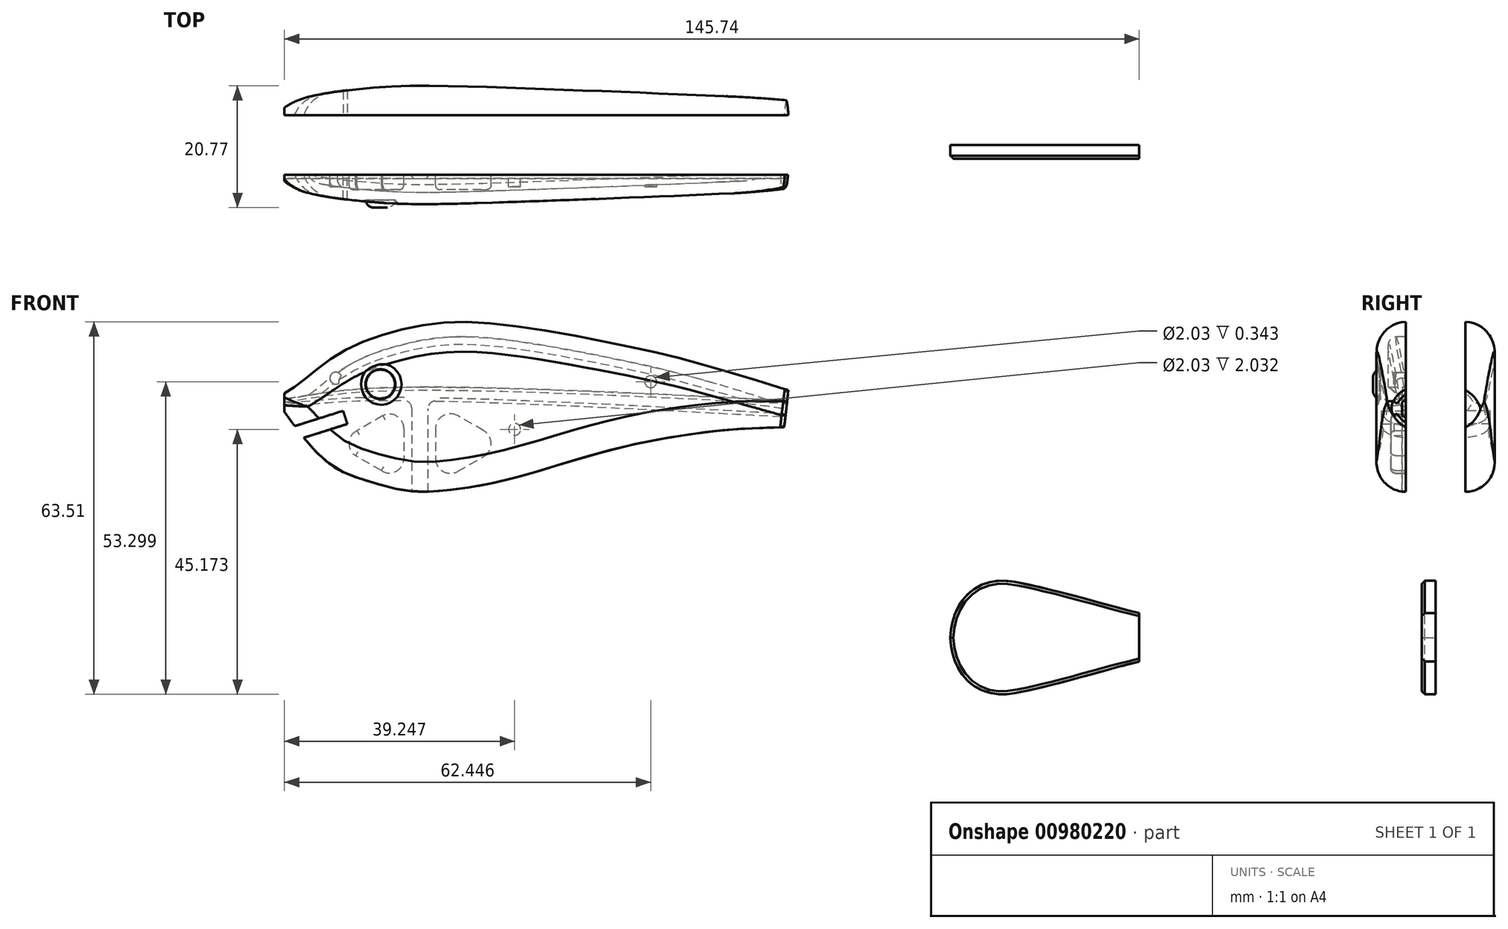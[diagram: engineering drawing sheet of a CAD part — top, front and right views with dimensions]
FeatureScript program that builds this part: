
annotation { "Feature Type Name" : "Feature", "Feature Type Description" : "" }
export const myFeature = defineFeature(function(context is Context, id is Id, definition is map)
    precondition{}
    {
        {
            var Q0;
            Q0=qCreatedBy(makeId("Front.planeOp"),FACE);
            var sketch = newSketch(context, id + "F0", { "sketchPlane" : qUnion([Q0])});
            skLineSegment(sketch, "E0", {"start": v(-42.86, 0) * mm, "end": v(42.86, 0) * mm});
            skSolve(sketch);
        }
        {
            var Q0;
            Q0=qCreatedBy(makeId("Front.planeOp"),FACE);
            var sketch = newSketch(context, id + "F1", { "sketchPlane" : qUnion([Q0])});
            skLineSegment(sketch, "E1", {"start": v(-42.86, -1.4) * mm, "end": v(-42.86, 1.77) * mm});
            skFitSpline(sketch, "E2", {"points": [v(-42.86, 1.77) * mm, v(-40.35, 3.39) * mm, v(-36.78, 6.26) * mm, v(-31.29, 9.73) * mm, v(-23.44, 12.5) * mm, v(-14.52, 13.9) * mm, v(-2.07, 13) * mm, v(15.45, 9.8) * mm, v(27.42, 6.96) * mm, v(43.06, 2.27) * mm], "startDerivative": vector(39.21, 23.39) * mm, "endDerivative": vector(112.18, -34.84) * mm});
            skLineSegment(sketch, "E3", {"start": v(43.06, 2.27) * mm, "end": v(42.36, -4.04) * mm});
            skFitSpline(sketch, "E4", {"points": [v(42.36, -4.04) * mm, v(32.37, -4.52) * mm, v(17.64, -6.76) * mm, v(5.02, -10.13) * mm, v(-6.94, -13.46) * mm, v(-16.36, -14.9) * mm, v(-21.97, -14.86) * mm, v(-29.24, -13.02) * mm, v(-34.41, -10.79) * mm, v(-38.97, -6.54) * mm, v(-42.86, -1.4) * mm], "startDerivative": vector(-88.65, -2.09) * mm, "endDerivative": vector(-43.74, 61.13) * mm});
            skSolve(sketch);
        }
        {
            var Q0;
            Q0 = qSketchRegion(id + "F1", true);
            extrude(context, id + "F2", {"entities" : qUnion([Q0]), "depth" : 10.16 * mm, "offsetDistance" : 25.4 * mm});
        }
        {
            var Q0;
            Q0=qCreatedBy(makeId("Top.planeOp"),FACE);
            var sketch = newSketch(context, id + "F3", { "sketchPlane" : qUnion([Q0])});
            skLineSegment(sketch, "E5", {"start": v(-42.86, 0) * mm, "end": v(-42.86, -3.14) * mm});
            skFitSpline(sketch, "E6", {"points": [v(-42.86, -3.14) * mm, v(-36.68, -1.52) * mm, v(-25.95, -0.28) * mm, v(-17.83, -0.07) * mm, v(-1.73, -0.51) * mm, v(26.04, -1.58) * mm, v(43.3, -2.37) * mm], "startDerivative": vector(48.92, 15.17) * mm, "endDerivative": vector(84.45, -4.03) * mm});
            skLineSegment(sketch, "E7", {"start": v(-42.86, 0) * mm, "end": v(-42.86, 3.25) * mm});
            skLineSegment(sketch, "E8", {"start": v(-42.86, 3.25) * mm, "end": v(43.3, 3.25) * mm});
            skLineSegment(sketch, "E9", {"start": v(43.3, 3.25) * mm, "end": v(43.3, -2.37) * mm});
            skFitSpline(sketch, "E10.MirrorCS", {"points": [v(-42.86, -7.02) * mm, v(-36.68, -8.64) * mm, v(-25.95, -9.88) * mm, v(-17.83, -10.1) * mm, v(-1.73, -9.65) * mm, v(26.04, -8.58) * mm, v(43.3, -7.79) * mm], "startDerivative": vector(48.92, -15.17) * mm, "endDerivative": vector(84.45, 4.03) * mm});
            skLineSegment(sketch, "E11.MirrorCS", {"start": v(-42.86, -7.02) * mm, "end": v(-42.86, -13.4) * mm});
            skLineSegment(sketch, "E12.MirrorCS", {"start": v(-42.86, -13.4) * mm, "end": v(43.3, -13.4) * mm});
            skLineSegment(sketch, "E13.MirrorCS", {"start": v(43.3, -13.4) * mm, "end": v(43.3, -7.79) * mm});
            skSolve(sketch);
        }
        {
            var Q0;
            Q0 = qSketchRegion(id + "F3", true);
            extrude(context, id + "F4", {"entities" : qUnion([Q0]), "operationType" : NewBodyOperationType.REMOVE, "endBound" : BoundingType.SYMMETRIC, "oppositeDirection" : true, "depth" : 152.4 * mm, "offsetDistance" : 25.4 * mm});
        }
        {
            var Q0;
            Q0=qCreatedBy(makeId("Top.planeOp"),FACE);
            var sketch = newSketch(context, id + "F5", { "sketchPlane" : qUnion([Q0])});
            skLineSegment(sketch, "E14.bottom", {"start": v(-44.5, -5.08) * mm, "end": v(45.7, -5.08) * mm});
            skLineSegment(sketch, "E14.top", {"start": v(-44.5, 11.17) * mm, "end": v(45.7, 11.17) * mm});
            skLineSegment(sketch, "E14.left", {"start": v(-44.5, -5.08) * mm, "end": v(-44.5, 11.17) * mm});
            skLineSegment(sketch, "E14.right", {"start": v(45.7, -5.08) * mm, "end": v(45.7, 11.17) * mm});
            skSolve(sketch);
        }
        {
            var Q0;
            Q0 = qSketchRegion(id + "F5", true);
            extrude(context, id + "F6", {"entities" : qUnion([Q0]), "operationType" : NewBodyOperationType.REMOVE, "endBound" : BoundingType.SYMMETRIC, "oppositeDirection" : true, "depth" : 152.4 * mm, "offsetDistance" : 25.4 * mm});
        }
        {
            var Q0;
            Q0=makeQuery(id+"F4.boolean.opBoolean","INTERSECT",EDGE,{"derivedFrom":[makeQuery(id+"F2.opExtrude","SWEPT_FACE",FACE,{"disambiguationData":[OSD([sQuery(id+"F1.wireOp",EDGE,"E2")])]}),makeQuery(id+"F4.opExtrude","SWEPT_FACE",FACE,{"disambiguationData":[OSD([sQuery(id+"F3.wireOp",EDGE,"E10.MirrorCS")])]})]});
            var Q1;
            Q1=makeQuery(id+"F4.boolean.opBoolean","INTERSECT",EDGE,{"derivedFrom":[makeQuery(id+"F2.opExtrude","SWEPT_FACE",FACE,{"disambiguationData":[OSD([sQuery(id+"F1.wireOp",EDGE,"E4")])]}),makeQuery(id+"F4.opExtrude","SWEPT_FACE",FACE,{"disambiguationData":[OSD([sQuery(id+"F3.wireOp",EDGE,"E10.MirrorCS")])]})]});
            fillet(context, id + "F7", {"entities" : qUnion([Q0, Q1]), "radius" : 5.08 * mm, "tangentPropagation" : true, "allowEdgeOverflow" : false});
        }
        {
            var Q0;
            Q0=qCreatedBy(makeId("Front.planeOp"),FACE);
            var sketch = newSketch(context, id + "F8", { "sketchPlane" : qUnion([Q0])});
            skLineSegment(sketch, "E15", {"start": v(-32.84, -1.24) * mm, "end": v(-47.55, -5.87) * mm});
            skLineSegment(sketch, "E16", {"start": v(-47.55, -5.87) * mm, "end": v(-46.84, -8.13) * mm});
            skLineSegment(sketch, "E17", {"start": v(-46.84, -8.13) * mm, "end": v(-32.13, -3.49) * mm});
            skLineSegment(sketch, "E18", {"start": v(-32.13, -3.49) * mm, "end": v(-32.84, -1.24) * mm});
            skSolve(sketch);
        }
        {
            var Q0;
            Q0 = qSketchRegion(id + "F8", true);
            extrude(context, id + "F9", {"entities" : qUnion([Q0]), "operationType" : NewBodyOperationType.REMOVE, "depth" : 25.4 * mm, "offsetDistance" : 25.4 * mm});
        }
        {
            var Q0;
            Q0=makeQuery(id+"F2.opExtrude","SWEPT_BODY",BODY,{"disambiguationData":[OSD([sQuery(id+"F1.wireOp",EDGE,"E1"),sQuery(id+"F1.wireOp",EDGE,"E2"),sQuery(id+"F1.wireOp",EDGE,"E3"),sQuery(id+"F1.wireOp",EDGE,"E4")])]});
            var Q1;
            Q1=qCreatedBy(makeId("Front.planeOp"),FACE);
            mirror(context, id + "F10", {"entities" : qUnion([Q0]), "mirrorPlane" : qUnion([Q1])});
        }
        {
            var Q0;
            Q0=qCreatedBy(makeId("Front.planeOp"),FACE);
            var sketch = newSketch(context, id + "F11", { "sketchPlane" : qUnion([Q0])});
            skLineSegment(sketch, "E19", {"start": v(102.87, -39.86) * mm, "end": v(102.87, -35.72) * mm});
            skFitSpline(sketch, "E20", {"points": [v(102.87, -35.72) * mm, v(94.2, -33.44) * mm, v(85.73, -31.27) * mm, v(82.22, -30.53) * mm, v(78.88, -30.22) * mm, v(75.16, -31.35) * mm, v(72.53, -33.83) * mm, v(71.19, -36.7) * mm, v(70.67, -39.9) * mm], "startDerivative": vector(-48.37, 11.41) * mm, "endDerivative": vector(-0.62, -33.43) * mm});
            skLineSegment(sketch, "E21", {"start": v(70.67, -39.9) * mm, "end": v(102.87, -39.86) * mm});
            skFitSpline(sketch, "E22.MirrorCS", {"points": [v(102.88, -44) * mm, v(94.22, -46.3) * mm, v(85.76, -48.5) * mm, v(82.25, -49.25) * mm, v(78.91, -49.57) * mm, v(75.2, -48.46) * mm, v(72.56, -45.98) * mm, v(71.2, -43.1) * mm, v(70.67, -39.9) * mm], "startDerivative": vector(-48.33, -11.57) * mm, "endDerivative": vector(-0.73, 33.43) * mm});
            skLineSegment(sketch, "E23.MirrorCS", {"start": v(102.87, -39.86) * mm, "end": v(102.88, -44) * mm});
            skSolve(sketch);
        }
        {
            var Q0;
            Q0 = qSketchRegion(id + "F11", true);
            extrude(context, id + "F12", {"entities" : qUnion([Q0]), "depth" : 2.34 * mm, "offsetDistance" : 25.4 * mm});
        }
        {
            var Q0;
            Q0=makeQuery(id+"F6.boolean.opBoolean","COPY",FACE,{"derivedFrom":makeQuery(id+"F6.opExtrude","SWEPT_FACE",FACE,{"disambiguationData":[OSD([sQuery(id+"F5.wireOp",EDGE,"E14.bottom")])]})});
            var sketch = newSketch(context, id + "F13", { "sketchPlane" : qUnion([Q0])});
            skLineSegment(sketch, "E24", {"start": v(42.86, 0.76) * mm, "end": v(42.86, -0.5) * mm});
            skLineSegment(sketch, "E25", {"start": v(-42.86, 0.5) * mm, "end": v(-42.56, -2.27) * mm});
            skFitSpline(sketch, "E26", {"points": [v(42.86, 0.76) * mm, v(28.16, 2.6) * mm, v(-42.86, 0.5) * mm], "startDerivative": vector(-45.97, 6.78) * mm, "endDerivative": vector(-118.14, -6) * mm});
            skFitSpline(sketch, "E27", {"points": [v(42.86, -0.5) * mm, v(28.16, 0.5) * mm, v(-42.56, -2.27) * mm], "startDerivative": vector(-46.03, 4.16) * mm, "endDerivative": vector(-117.54, -6.6) * mm});
            skLineSegment(sketch, "E28", {"start": v(18.37, -17.26) * mm, "end": v(18.37, -0.84) * mm});
            skLineSegment(sketch, "E29", {"start": v(21.17, -0.75) * mm, "end": v(21.17, -17.26) * mm});
            skLineSegment(sketch, "E30", {"start": v(21.17, -17.26) * mm, "end": v(18.37, -17.26) * mm});
            skFitSpline(sketch, "E31.trimOffspring", {"points": [v(42.86, -0.5) * mm, v(28.16, 0.5) * mm, v(-42.56, -2.27) * mm], "startDerivative": vector(-46.03, 4.16) * mm, "endDerivative": vector(-117.54, -6.6) * mm});
            skPoint(sketch, "E32.visualSharp", {"position": v(18.37, 0.46) * mm});
            skArc(sketch, "E32.filletArc", {"start": v(18.37, -0.84) * mm, "mid": v(18, 0.07) * mm, "end": v(17.08, 0.43) * mm});
            skPoint(sketch, "E33.visualSharp", {"position": v(21.17, 0.5) * mm});
            skArc(sketch, "E33.filletArc", {"start": v(22.43, 0.52) * mm, "mid": v(21.54, 0.14) * mm, "end": v(21.17, -0.75) * mm});
            skSolve(sketch);
        }
        {
            var Q0;
            Q0 = qSketchRegion(id + "F13", true);
            extrude(context, id + "F14", {"entities" : qUnion([Q0]), "operationType" : NewBodyOperationType.REMOVE, "oppositeDirection" : true, "depth" : 0.64 * mm, "offsetDistance" : 25.4 * mm});
        }
        {
            var Q0;
            Q0=makeQuery(id+"F14.boolean.opBoolean","COPY",EDGE,{"derivedFrom":makeQuery(id+"F14.opExtrude","CAP_EDGE",EDGE,{"disambiguationData":[OSD([sQuery(id+"F13.wireOp",EDGE,"E26")])],"isStart":false})});
            var Q1;
            Q1=makeQuery(id+"F14.boolean.opBoolean","COPY",EDGE,{"derivedFrom":makeQuery(id+"F14.opExtrude","CAP_EDGE",EDGE,{"disambiguationData":[OSD([sQuery(id+"F13.wireOp",EDGE,"E27")])],"isStart":false})});
            var Q2;
            Q2=makeQuery(id+"F14.boolean.opBoolean","COPY",EDGE,{"derivedFrom":makeQuery(id+"F14.opExtrude","CAP_EDGE",EDGE,{"disambiguationData":[OSD([sQuery(id+"F13.wireOp",EDGE,"E32.filletArc")])],"isStart":false})});
            fillet(context, id + "F15", {"entities" : qUnion([Q0, Q1, Q2]), "radius" : 0.5 * mm, "tangentPropagation" : true, "allowEdgeOverflow" : false});
        }
        {
            var Q0;
            {var subQ0=makeQuery(id+"F4.opExtrude","SWEPT_FACE",FACE,{"disambiguationData":[OSD([sQuery(id+"F3.wireOp",EDGE,"E10.MirrorCS")])]});Q0=makeQuery(id+"F7.opFillet","BLEND_EDGE",EDGE,{"disambiguationData":[OD(0.0)],"blendedFrom":[makeQuery(id+"F4.boolean.opBoolean","INTERSECT",EDGE,{"derivedFrom":[makeQuery(id+"F2.opExtrude","SWEPT_FACE",FACE,{"disambiguationData":[OSD([sQuery(id+"F1.wireOp",EDGE,"E2")])]}),subQ0]}),makeQuery(id+"F4.boolean.opBoolean","INTERSECT",EDGE,{"derivedFrom":[makeQuery(id+"F2.opExtrude","SWEPT_FACE",FACE,{"disambiguationData":[OSD([sQuery(id+"F1.wireOp",EDGE,"E4")])]}),subQ0]})],"blendedInto":[]});}
            fillet(context, id + "F16", {"entities" : qUnion([Q0]), "radius" : 1.27 * mm, "tangentPropagation" : true, "allowEdgeOverflow" : false});
        }
        {
            var Q0;
            {var subQ0=makeQuery(id+"F4.opExtrude","SWEPT_FACE",FACE,{"disambiguationData":[OSD([sQuery(id+"F3.wireOp",EDGE,"E10.MirrorCS")])]});Q0=makeQuery(id+"F7.opFillet","BLEND_EDGE",EDGE,{"disambiguationData":[OD(1.0)],"blendedFrom":[makeQuery(id+"F4.boolean.opBoolean","INTERSECT",EDGE,{"derivedFrom":[makeQuery(id+"F2.opExtrude","SWEPT_FACE",FACE,{"disambiguationData":[OSD([sQuery(id+"F1.wireOp",EDGE,"E2")])]}),subQ0]}),makeQuery(id+"F4.boolean.opBoolean","INTERSECT",EDGE,{"derivedFrom":[makeQuery(id+"F2.opExtrude","SWEPT_FACE",FACE,{"disambiguationData":[OSD([sQuery(id+"F1.wireOp",EDGE,"E4")])]}),subQ0]})],"blendedInto":[]});}
            fillet(context, id + "F17", {"entities" : qUnion([Q0]), "radius" : 2.54 * mm, "tangentPropagation" : true, "allowEdgeOverflow" : false});
        }
        {
            var Q0;
            Q0=makeQuery(id+"F14.boolean.opBoolean","SPLIT",FACE,{"disambiguationData":[TD([makeQuery(id+"F14.opExtrude","SWEPT_FACE",FACE,{"disambiguationData":[OSD([sQuery(id+"F13.wireOp",EDGE,"E26")])]})])],"derivedFrom":makeQuery(id+"F6.boolean.opBoolean","COPY",FACE,{"derivedFrom":makeQuery(id+"F6.opExtrude","SWEPT_FACE",FACE,{"disambiguationData":[OSD([sQuery(id+"F5.wireOp",EDGE,"E14.bottom")])]})})});
            var sketch = newSketch(context, id + "F18", { "sketchPlane" : qUnion([Q0])});
            skFitSpline(sketch, "E34.0", {"points": [v(41.56, -0.41) * mm, v(41.36, -0.3) * mm, v(40.94, -0.04) * mm, v(40.28, 0.37) * mm, v(39.7, 0.74) * mm, v(39.22, 1.08) * mm, v(38.85, 1.34) * mm, v(38.48, 1.62) * mm, v(38, 2) * mm, v(37.4, 2.49) * mm, v(36.67, 3.09) * mm, v(35.7, 3.89) * mm, v(34.45, 4.86) * mm, v(32.82, 5.99) * mm, v(31.33, 6.86) * mm, v(30.07, 7.5) * mm, v(28.74, 8.11) * mm, v(26.95, 8.8) * mm, v(25.04, 9.42) * mm, v(23.48, 9.86) * mm, v(21.9, 10.27) * mm, v(19.93, 10.7) * mm, v(17.54, 11.1) * mm, v(15.5, 11.3) * mm, v(13.82, 11.38) * mm, v(12.08, 11.4) * mm, v(9.8, 11.32) * mm, v(6.86, 11.07) * mm, v(4.21, 10.75) * mm, v(1.97, 10.43) * mm, v(-0.36, 10.07) * mm, v(-3.39, 9.56) * mm, v(-7.08, 8.9) * mm, v(-10.1, 8.3) * mm, v(-12.44, 7.84) * mm, v(-14.12, 7.5) * mm, v(-15.74, 7.15) * mm, v(-17.78, 6.72) * mm, v(-20.19, 6.18) * mm, v(-22.97, 5.5) * mm, v(-25.32, 4.9) * mm, v(-27.28, 4.36) * mm, v(-29.33, 3.79) * mm, v(-32, 3) * mm, v(-35.35, 2) * mm, v(-38.8, 0.93) * mm, v(-41.14, 0.2) * mm, v(-42.3, -0.15) * mm]});
            skLineSegment(sketch, "E35", {"start": v(-7, 7.84) * mm, "end": v(-7, 5.87) * mm});
            skLineSegment(sketch, "E36", {"start": v(-5.74, 4.6) * mm, "end": v(30.46, 4.6) * mm});
            skPoint(sketch, "E37.visualSharp", {"position": v(34.77, 4.6) * mm});
            skArc(sketch, "E37.filletArc", {"start": v(30.46, 4.6) * mm, "mid": v(31.7, 5.56) * mm, "end": v(31.06, 7) * mm});
            skPoint(sketch, "E38.visualSharp", {"position": v(-7, 8.9) * mm});
            skArc(sketch, "E38.filletArc", {"start": v(-5.97, 9.1) * mm, "mid": v(-6.71, 8.65) * mm, "end": v(-7, 7.84) * mm});
            skPoint(sketch, "E39.visualSharp", {"position": v(-7, 4.6) * mm});
            skArc(sketch, "E39.filletArc", {"start": v(-7, 5.87) * mm, "mid": v(-6.64, 4.97) * mm, "end": v(-5.74, 4.6) * mm});
            skSolve(sketch);
        }
        {
            var Q0;
            Q0=makeQuery(id+"F18.imprint","IMPRINT",FACE,{"disambiguationData":[TD([[makeQuery(id+"F18.imprint","IMPRINT",EDGE,{"derivedFrom":sQuery(id+"F18.wireOp",EDGE,"E34.0")}),1.0]])]});
            var Q1;
            Q1=makeQuery(id+"F4.boolean.opBoolean","COPY",FACE,{"derivedFrom":makeQuery(id+"F4.opExtrude","SWEPT_FACE",FACE,{"disambiguationData":[OSD([sQuery(id+"F3.wireOp",EDGE,"E10.MirrorCS")])]})});
            extrude(context, id + "F19", {"entities" : qUnion([Q0]), "operationType" : NewBodyOperationType.REMOVE, "endBound" : BoundingType.UP_TO_SURFACE, "oppositeDirection" : true, "depth" : 25.4 * mm, "endBoundEntityFace" : qUnion([Q1]), "hasOffset" : true, "offsetDistance" : 2.03 * mm});
        }
        {
            var Q0;
            Q0=makeQuery(id+"F19.boolean.opBoolean","COPY",EDGE,{"derivedFrom":makeQuery(id+"F19.opExtrude","CAP_EDGE",EDGE,{"disambiguationData":[OSD([sQuery(id+"F18.wireOp",EDGE,"E34.0")])],"isStart":false})});
            fillet(context, id + "F20", {"entities" : qUnion([Q0]), "radius" : 1.27 * mm, "tangentPropagation" : true, "allowEdgeOverflow" : false});
        }
        {
            var Q0;
            Q0=makeQuery(id+"F14.boolean.opBoolean","SPLIT",FACE,{"disambiguationData":[TD([makeQuery(id+"F14.opExtrude","SWEPT_FACE",FACE,{"disambiguationData":[OSD([sQuery(id+"F13.wireOp",EDGE,"E28")])]})])],"derivedFrom":makeQuery(id+"F6.boolean.opBoolean","COPY",FACE,{"derivedFrom":makeQuery(id+"F6.opExtrude","SWEPT_FACE",FACE,{"disambiguationData":[OSD([sQuery(id+"F5.wireOp",EDGE,"E14.bottom")])]})})});
            var sketch = newSketch(context, id + "F21", { "sketchPlane" : qUnion([Q0])});
            skArc(sketch, "E40", {"start": v(26.1, -2.07) * mm, "mid": v(23.68, -2.17) * mm, "end": v(22.5, -4.28) * mm});
            skArc(sketch, "E41", {"start": v(22.5, -9.36) * mm, "mid": v(23.8, -11.54) * mm, "end": v(26.33, -11.44) * mm});
            skArc(sketch, "E42", {"start": v(30.73, -8.9) * mm, "mid": v(31.85, -6.69) * mm, "end": v(30.5, -4.61) * mm});
            skLineSegment(sketch, "E43", {"start": v(22.5, -4.28) * mm, "end": v(22.5, -9.36) * mm});
            skLineSegment(sketch, "E44", {"start": v(26.1, -2.07) * mm, "end": v(30.5, -4.61) * mm});
            skLineSegment(sketch, "E45", {"start": v(26.33, -11.44) * mm, "end": v(30.73, -8.9) * mm});
            skArc(sketch, "E46", {"start": v(17.1, -4.28) * mm, "mid": v(15.83, -2.08) * mm, "end": v(13.3, -2.08) * mm});
            skArc(sketch, "E47", {"start": v(13.3, -11.56) * mm, "mid": v(15.83, -11.56) * mm, "end": v(17.1, -9.36) * mm});
            skArc(sketch, "E48", {"start": v(8.9, -4.62) * mm, "mid": v(7.62, -6.82) * mm, "end": v(8.9, -9.02) * mm});
            skLineSegment(sketch, "E49", {"start": v(17.1, -4.28) * mm, "end": v(17.1, -9.36) * mm});
            skLineSegment(sketch, "E50", {"start": v(13.3, -11.56) * mm, "end": v(8.9, -9.02) * mm});
            skLineSegment(sketch, "E51", {"start": v(8.9, -4.62) * mm, "end": v(13.3, -2.08) * mm});
            skSolve(sketch);
        }
        {
            var Q0;
            Q0 = qSketchRegion(id + "F21", true);
            extrude(context, id + "F22", {"entities" : qUnion([Q0]), "operationType" : NewBodyOperationType.REMOVE, "oppositeDirection" : true, "depth" : 2.54 * mm, "offsetDistance" : 25.4 * mm});
        }
        {
            var Q0;
            Q0=makeQuery(id+"F22.boolean.opBoolean","COPY",EDGE,{"derivedFrom":makeQuery(id+"F22.opExtrude","CAP_EDGE",EDGE,{"disambiguationData":[OSD([sQuery(id+"F21.wireOp",EDGE,"E51")])],"isStart":false})});
            var Q1;
            Q1=makeQuery(id+"F22.boolean.opBoolean","COPY",EDGE,{"derivedFrom":makeQuery(id+"F22.opExtrude","CAP_EDGE",EDGE,{"disambiguationData":[OSD([sQuery(id+"F21.wireOp",EDGE,"E43")])],"isStart":false})});
            var Q2;
            Q2=makeQuery(id+"F22.boolean.opBoolean","COPY",EDGE,{"derivedFrom":makeQuery(id+"F22.opExtrude","CAP_EDGE",EDGE,{"disambiguationData":[OSD([sQuery(id+"F21.wireOp",EDGE,"E44")])],"isStart":false})});
            var Q3;
            Q3=makeQuery(id+"F22.boolean.opBoolean","COPY",EDGE,{"derivedFrom":makeQuery(id+"F22.opExtrude","CAP_EDGE",EDGE,{"disambiguationData":[OSD([sQuery(id+"F21.wireOp",EDGE,"E42")])],"isStart":false})});
            fillet(context, id + "F23", {"entities" : qUnion([Q0, Q1, Q2, Q3]), "radius" : 0.76 * mm, "tangentPropagation" : true, "allowEdgeOverflow" : false});
        }
        {
            var Q0;
            Q0=makeQuery(id+"F14.boolean.opBoolean","SPLIT",FACE,{"disambiguationData":[TD([makeQuery(id+"F14.opExtrude","SWEPT_FACE",FACE,{"disambiguationData":[OSD([sQuery(id+"F13.wireOp",EDGE,"E28")])]})])],"derivedFrom":makeQuery(id+"F6.boolean.opBoolean","COPY",FACE,{"derivedFrom":makeQuery(id+"F6.opExtrude","SWEPT_FACE",FACE,{"disambiguationData":[OSD([sQuery(id+"F5.wireOp",EDGE,"E14.bottom")])]})})});
            var sketch = newSketch(context, id + "F24", { "sketchPlane" : qUnion([Q0])});
            skCircle(sketch, "E52", {"center": v(3.61, -4.4) * mm, "radius": 1.02 * mm});
            skCircle(sketch, "E53", {"center": v(34.1, 4.34) * mm, "radius": 1.02 * mm});
            skCircle(sketch, "E54", {"center": v(-19.59, 3.72) * mm, "radius": 1.02 * mm});
            skSolve(sketch);
        }
        {
            var Q0;
            Q0 = qSketchRegion(id + "F24", true);
            extrude(context, id + "F25", {"entities" : qUnion([Q0]), "operationType" : NewBodyOperationType.REMOVE, "oppositeDirection" : true, "depth" : 2.03 * mm, "offsetDistance" : 25.4 * mm});
        }
        {
            var Q0;
            Q0=qCreatedBy(makeId("Front.planeOp"),FACE);
            cPlane(context, id + "F26", {"entities" : qUnion([Q0]), "cplaneType" : CPlaneType.OFFSET, "offset" : 25.4 * mm, "width" : 152.4 * mm, "height" : 152.4 * mm});
        }
        {
            var Q0;
            Q0=qCreatedBy(id+"F26.planeOp",FACE);
            var sketch = newSketch(context, id + "F27", { "sketchPlane" : qUnion([Q0])});
            skCircle(sketch, "E55", {"center": v(-26.5, 3.3) * mm, "radius": 2.54 * mm});
            skSolve(sketch);
        }
        {
            var Q0;
            Q0 = qSketchRegion(id + "F27", true);
            extrude(context, id + "F28", {"entities" : qUnion([Q0]), "operationType" : NewBodyOperationType.REMOVE, "oppositeDirection" : true, "depth" : 16 * mm, "offsetDistance" : 25.4 * mm});
        }
        {
            var Q0;
            Q0=makeQuery(id+"F28.boolean.opBoolean","COPY",FACE,{"derivedFrom":makeQuery(id+"F28.opExtrude","CAP_FACE",FACE,{"disambiguationData":[OSD([sQuery(id+"F27.wireOp",EDGE,"E55")])],"isStart":false})});
            var sketch = newSketch(context, id + "F29", { "sketchPlane" : qUnion([Q0])});
            skCircle(sketch, "E56", {"center": v(-26.5, 3.3) * mm, "radius": 2.48 * mm});
            skSolve(sketch);
        }
        {
            var Q0;
            Q0 = qSketchRegion(id + "F29", true);
            extrude(context, id + "F30", {"entities" : qUnion([Q0]), "operationType" : NewBodyOperationType.ADD, "depth" : 1.27 * mm, "offsetDistance" : 25.4 * mm});
        }
        {
            var Q0;
            Q0=makeQuery(id+"F28.boolean.opBoolean","INTERSECT",EDGE,{"derivedFrom":[makeQuery(id+"F4.boolean.opBoolean","COPY",FACE,{"derivedFrom":makeQuery(id+"F4.opExtrude","SWEPT_FACE",FACE,{"disambiguationData":[OSD([sQuery(id+"F3.wireOp",EDGE,"E10.MirrorCS")])]})}),makeQuery(id+"F28.opExtrude","SWEPT_FACE",FACE,{"disambiguationData":[OSD([sQuery(id+"F27.wireOp",EDGE,"E55")])]})]});
            fillet(context, id + "F31", {"entities" : qUnion([Q0]), "radius" : 1.27 * mm, "tangentPropagation" : true, "allowEdgeOverflow" : false});
        }
        {
            var Q0;
            Q0=makeQuery(id+"F30.opExtrude","CAP_EDGE",EDGE,{"disambiguationData":[OSD([sQuery(id+"F29.wireOp",EDGE,"E56")])],"isStart":false});
            fillet(context, id + "F32", {"entities" : qUnion([Q0]), "radius" : 1.27 * mm, "tangentPropagation" : true, "allowEdgeOverflow" : false});
        }
        {
            var Q0;
            Q0=makeQuery(id+"F7.opFillet","BLEND_EDGE",EDGE,{"blendedFrom":[makeQuery(id+"F4.boolean.opBoolean","INTERSECT",EDGE,{"derivedFrom":[makeQuery(id+"F2.opExtrude","SWEPT_FACE",FACE,{"disambiguationData":[OSD([sQuery(id+"F1.wireOp",EDGE,"E2")])]}),makeQuery(id+"F4.opExtrude","SWEPT_FACE",FACE,{"disambiguationData":[OSD([sQuery(id+"F3.wireOp",EDGE,"E10.MirrorCS")])]})]}),makeQuery(id+"F2.opExtrude","SWEPT_FACE",FACE,{"disambiguationData":[OSD([sQuery(id+"F1.wireOp",EDGE,"E3")])]})],"blendedInto":[makeQuery(id+"F2.opExtrude","SWEPT_FACE",FACE,{"disambiguationData":[OSD([sQuery(id+"F1.wireOp",EDGE,"E3")])]})]});
            fillet(context, id + "F33", {"entities" : qUnion([Q0]), "radius" : 0.76 * mm, "tangentPropagation" : true, "allowEdgeOverflow" : false});
        }
        {
            var Q0;
            Q0=makeQuery(id+"F12.opExtrude","CAP_EDGE",EDGE,{"disambiguationData":[OSD([sQuery(id+"F11.wireOp",EDGE,"E20")])],"isStart":false});
            var Q1;
            Q1=makeQuery(id+"F12.opExtrude","CAP_EDGE",EDGE,{"disambiguationData":[OSD([sQuery(id+"F11.wireOp",EDGE,"E22.MirrorCS")])],"isStart":false});
            chamfer(context, id + "F34", {"entities" : qUnion([Q0, Q1]), "width" : 0.5 * mm, "tangentPropagation" : true});
        }
    });
